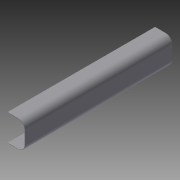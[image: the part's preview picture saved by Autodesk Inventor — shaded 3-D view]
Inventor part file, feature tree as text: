
AUTODESK INVENTOR PART (.ipt)
format: ipt  version: 2015 SP1 (Build 190203100, 203)  size: 123,904 bytes
history: native  units: in
note: dims shown in document units (in); Inventor stores cm internally (conversion verified against a paired STEP export)
features: extrude x2, sketch x2, projected_geometry x1
ambient origin geometry x8: Origin, YZ Plane, XZ Plane, XY Plane, X Axis, Y Axis, Z Axis, Center Point
bodies: Solid1 (feature_tree)
feature tree (5):
  extrude  "Extrusion1"  Depth=5.0in
  extrude  "Extrusion2"  Depth=5.0in
  sketch  "Sketch1"  dims[d0=0.75in d1=5.0in]
  sketch  "Sketch2"  dims[d2=2.5in d3=5.0in d4=2.0in d5=0.05in d6=2.0in d7=0.05in d8=45.0deg d9=1.25in d10=45.0deg d11=1.25in d12=0.05in d13=2.5in d14=1.3in d15=1.3in d16=28.0in d17=0.0in d18=0.05in d19=1.0in d20=0.05in d21=1.0in d22=28.0in d23=0.0in]
  projected_geometry  "Projected Loop1"
